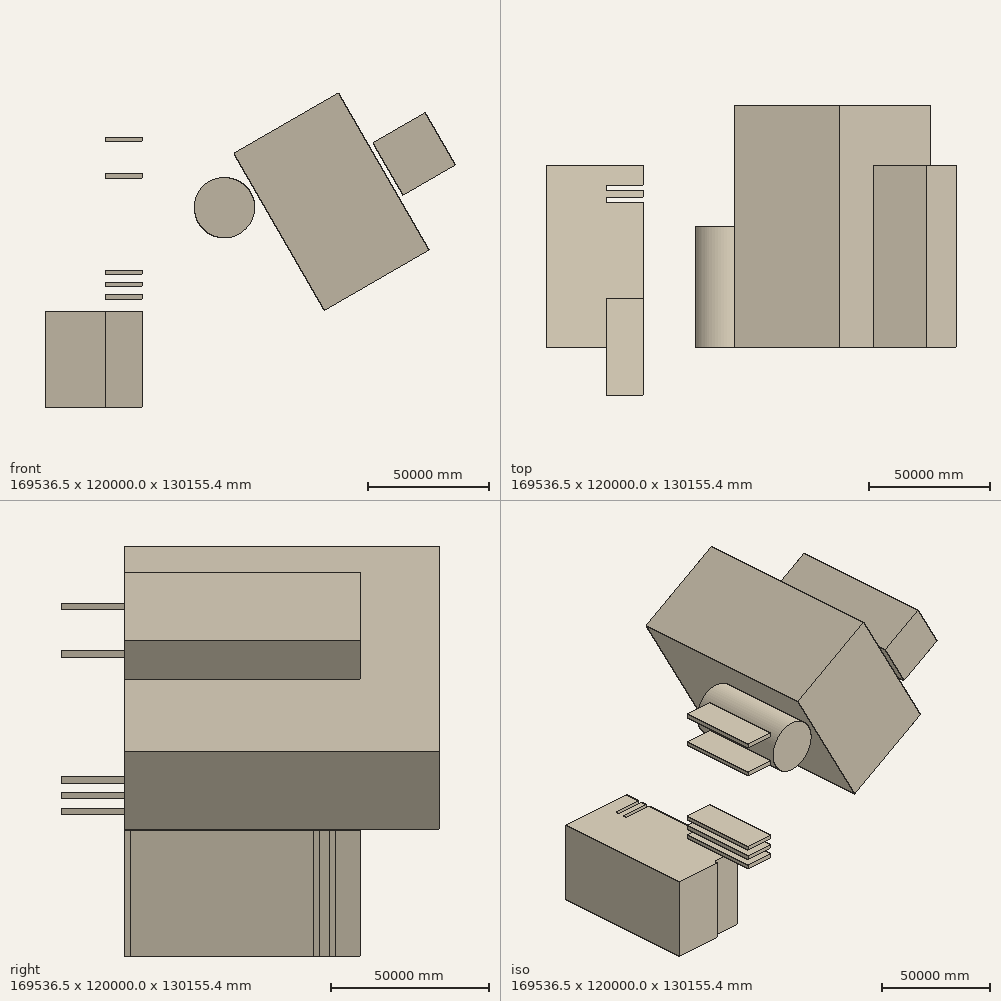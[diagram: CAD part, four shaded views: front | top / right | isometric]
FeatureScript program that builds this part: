
annotation { "Feature Type Name" : "Feature", "Feature Type Description" : "" }
export const myFeature = defineFeature(function(context is Context, id is Id, definition is map)
    precondition{}
    {
        {
            var Q0;
            Q0=qCreatedBy(makeId("Top.planeOp"),FACE);
            var sketch = newSketch(context, id + "F0", { "sketchPlane" : qUnion([Q0])});
            skLineSegment(sketch, "E0.bottom", {"start": v(20000, -20000) * mm, "end": v(-20000, -20000) * mm});
            skLineSegment(sketch, "E0.top", {"start": v(20000, 20000) * mm, "end": v(-20000, 20000) * mm});
            skLineSegment(sketch, "E0.left", {"start": v(20000, -20000) * mm, "end": v(20000, 20000) * mm});
            skLineSegment(sketch, "E0.right", {"start": v(-20000, -20000) * mm, "end": v(-20000, 20000) * mm});
            skPoint(sketch, "E0.middle", {"position": v(0, 0) * mm});
            skSolve(sketch);
        }
        {
            var Q0;
            Q0=makeQuery(id+"F0.imprint","IMPRINT",FACE,{"disambiguationData":[TD([[makeQuery(id+"F0.imprint","IMPRINT",EDGE,{"derivedFrom":sQuery(id+"F0.wireOp",EDGE,"E0.bottom")}),-1.0]])]});
            extrude(context, id + "F1", {"entities" : qUnion([Q0]), "depth" : 75000 * mm, "offsetDistance" : 25 * mm});
        }
        {
            var Q0;
            Q0=makeQuery(id+"F1.opExtrude","CAP_FACE",FACE,{"disambiguationData":[OSD([sQuery(id+"F0.wireOp",EDGE,"E0.bottom"),sQuery(id+"F0.wireOp",EDGE,"E0.top"),sQuery(id+"F0.wireOp",EDGE,"E0.left"),sQuery(id+"F0.wireOp",EDGE,"E0.right")])],"isStart":true});
            var sketch = newSketch(context, id + "F2", { "sketchPlane" : qUnion([Q0])});
            skLineSegment(sketch, "E1.bottom", {"start": v(20000, 20000) * mm, "end": v(5000, 20000) * mm});
            skLineSegment(sketch, "E1.top", {"start": v(20000, -20000) * mm, "end": v(5000, -20000) * mm});
            skLineSegment(sketch, "E1.left", {"start": v(20000, 20000) * mm, "end": v(20000, -20000) * mm});
            skLineSegment(sketch, "E1.right", {"start": v(5000, 20000) * mm, "end": v(5000, -20000) * mm});
            skSolve(sketch);
        }
        {
            var Q0;
            Q0=makeQuery(id+"F2.imprint","IMPRINT",FACE,{"disambiguationData":[TD([[makeQuery(id+"F2.imprint","IMPRINT",EDGE,{"derivedFrom":sQuery(id+"F2.wireOp",EDGE,"E1.bottom")}),1.0]])]});
            extrude(context, id + "F3", {"entities" : qUnion([Q0]), "oppositeDirection" : true, "depth" : 2000 * mm, "offsetDistance" : 25 * mm});
        }
        {
            var Q0;
            Q0=makeQuery(id+"F3.opExtrude","SWEPT_BODY",BODY,{"disambiguationData":[OSD([sQuery(id+"F2.wireOp",EDGE,"E1.bottom"),sQuery(id+"F2.wireOp",EDGE,"E1.top"),sQuery(id+"F2.wireOp",EDGE,"E1.left"),sQuery(id+"F2.wireOp",EDGE,"E1.right")])]});
            transform(context, id + "F4", {"entities" : qUnion([Q0]), "transformType" : TransformType.TRANSLATION_3D, "dx" : 0 * mm, "dy" : 0 * mm, "dz" : 5000 * mm, "makeCopy" : true});
        }
        {
            var Q0;
            Q0=makeQuery(id+"F4.opPattern","COPY",BODY,{"derivedFrom":makeQuery(id+"F3.opExtrude","SWEPT_BODY",BODY,{"disambiguationData":[OSD([sQuery(id+"F2.wireOp",EDGE,"E1.bottom"),sQuery(id+"F2.wireOp",EDGE,"E1.top"),sQuery(id+"F2.wireOp",EDGE,"E1.left"),sQuery(id+"F2.wireOp",EDGE,"E1.right")])]}),"instanceName":"1"});
            transform(context, id + "F5", {"entities" : qUnion([Q0]), "transformType" : TransformType.TRANSLATION_3D, "dx" : 0 * mm, "dy" : 0 * mm, "dz" : 5000 * mm, "makeCopy" : true});
        }
        {
            var Q0;
            Q0=makeQuery(id+"F5.opPattern","COPY",BODY,{"derivedFrom":makeQuery(id+"F4.opPattern","COPY",BODY,{"derivedFrom":makeQuery(id+"F3.opExtrude","SWEPT_BODY",BODY,{"disambiguationData":[OSD([sQuery(id+"F2.wireOp",EDGE,"E1.bottom"),sQuery(id+"F2.wireOp",EDGE,"E1.top"),sQuery(id+"F2.wireOp",EDGE,"E1.left"),sQuery(id+"F2.wireOp",EDGE,"E1.right")])]}),"instanceName":"1"}),"instanceName":"1"});
            transform(context, id + "F6", {"entities" : qUnion([Q0]), "transformType" : TransformType.TRANSLATION_3D, "dx" : 0 * mm, "dy" : 0 * mm, "dz" : 5000 * mm, "makeCopy" : true});
        }
        {
            var Q0;
            Q0=makeQuery(id+"F3.opExtrude","SWEPT_BODY",BODY,{"disambiguationData":[OSD([sQuery(id+"F2.wireOp",EDGE,"E1.bottom"),sQuery(id+"F2.wireOp",EDGE,"E1.top"),sQuery(id+"F2.wireOp",EDGE,"E1.left"),sQuery(id+"F2.wireOp",EDGE,"E1.right")])]});
            var Q1;
            Q1=makeQuery(id+"F4.opPattern","COPY",BODY,{"derivedFrom":makeQuery(id+"F3.opExtrude","SWEPT_BODY",BODY,{"disambiguationData":[OSD([sQuery(id+"F2.wireOp",EDGE,"E1.bottom"),sQuery(id+"F2.wireOp",EDGE,"E1.top"),sQuery(id+"F2.wireOp",EDGE,"E1.left"),sQuery(id+"F2.wireOp",EDGE,"E1.right")])]}),"instanceName":"1"});
            var Q2;
            Q2=makeQuery(id+"F5.opPattern","COPY",BODY,{"derivedFrom":makeQuery(id+"F4.opPattern","COPY",BODY,{"derivedFrom":makeQuery(id+"F3.opExtrude","SWEPT_BODY",BODY,{"disambiguationData":[OSD([sQuery(id+"F2.wireOp",EDGE,"E1.bottom"),sQuery(id+"F2.wireOp",EDGE,"E1.top"),sQuery(id+"F2.wireOp",EDGE,"E1.left"),sQuery(id+"F2.wireOp",EDGE,"E1.right")])]}),"instanceName":"1"}),"instanceName":"1"});
            var Q3;
            Q3=makeQuery(id+"F6.opPattern","COPY",BODY,{"derivedFrom":makeQuery(id+"F5.opPattern","COPY",BODY,{"derivedFrom":makeQuery(id+"F4.opPattern","COPY",BODY,{"derivedFrom":makeQuery(id+"F3.opExtrude","SWEPT_BODY",BODY,{"disambiguationData":[OSD([sQuery(id+"F2.wireOp",EDGE,"E1.bottom"),sQuery(id+"F2.wireOp",EDGE,"E1.top"),sQuery(id+"F2.wireOp",EDGE,"E1.left"),sQuery(id+"F2.wireOp",EDGE,"E1.right")])]}),"instanceName":"1"}),"instanceName":"1"}),"instanceName":"1"});
            transform(context, id + "F7", {"entities" : qUnion([Q0, Q1, Q2, Q3]), "transformType" : TransformType.TRANSLATION_3D, "dx" : 0 * mm, "dy" : 0 * mm, "dz" : 55000 * mm, "makeCopy" : true});
        }
        {
            var Q0;
            Q0=makeQuery(id+"F3.opExtrude","SWEPT_BODY",BODY,{"disambiguationData":[OSD([sQuery(id+"F2.wireOp",EDGE,"E1.bottom"),sQuery(id+"F2.wireOp",EDGE,"E1.top"),sQuery(id+"F2.wireOp",EDGE,"E1.left"),sQuery(id+"F2.wireOp",EDGE,"E1.right")])]});
            var Q1;
            Q1=makeQuery(id+"F7.opPattern","COPY",BODY,{"derivedFrom":makeQuery(id+"F5.opPattern","COPY",BODY,{"derivedFrom":makeQuery(id+"F4.opPattern","COPY",BODY,{"derivedFrom":makeQuery(id+"F3.opExtrude","SWEPT_BODY",BODY,{"disambiguationData":[OSD([sQuery(id+"F2.wireOp",EDGE,"E1.bottom"),sQuery(id+"F2.wireOp",EDGE,"E1.top"),sQuery(id+"F2.wireOp",EDGE,"E1.left"),sQuery(id+"F2.wireOp",EDGE,"E1.right")])]}),"instanceName":"1"}),"instanceName":"1"}),"instanceName":"1"});
            var Q2;
            Q2=makeQuery(id+"F7.opPattern","COPY",BODY,{"derivedFrom":makeQuery(id+"F4.opPattern","COPY",BODY,{"derivedFrom":makeQuery(id+"F3.opExtrude","SWEPT_BODY",BODY,{"disambiguationData":[OSD([sQuery(id+"F2.wireOp",EDGE,"E1.bottom"),sQuery(id+"F2.wireOp",EDGE,"E1.top"),sQuery(id+"F2.wireOp",EDGE,"E1.left"),sQuery(id+"F2.wireOp",EDGE,"E1.right")])]}),"instanceName":"1"}),"instanceName":"1"});
            var Q3;
            Q3=makeQuery(id+"F1.opExtrude","SWEPT_BODY",BODY,{"disambiguationData":[OSD([sQuery(id+"F0.wireOp",EDGE,"E0.bottom"),sQuery(id+"F0.wireOp",EDGE,"E0.top"),sQuery(id+"F0.wireOp",EDGE,"E0.left"),sQuery(id+"F0.wireOp",EDGE,"E0.right")])]});
            booleanBodies(context, id + "F8", {"operationType" : BooleanOperationType.SUBTRACTION, "tools" : qUnion([Q0, Q1, Q2]), "targets" : qUnion([Q3])});
        }
        {
            var Q0;
            Q0=qCreatedBy(makeId("Top.planeOp"),FACE);
            var sketch = newSketch(context, id + "F9", { "sketchPlane" : qUnion([Q0])});
            skLineSegment(sketch, "E2.bottom", {"start": v(130000, -37500) * mm, "end": v(80000, -37500) * mm});
            skLineSegment(sketch, "E2.top", {"start": v(130000, 37500) * mm, "end": v(80000, 37500) * mm});
            skLineSegment(sketch, "E2.left", {"start": v(130000, -37500) * mm, "end": v(130000, 37500) * mm});
            skLineSegment(sketch, "E2.right", {"start": v(80000, -37500) * mm, "end": v(80000, 37500) * mm});
            skPoint(sketch, "E2.middle", {"position": v(105000, 0) * mm});
            skLineSegment(sketch, "E3.bottom", {"start": v(157000, 12500) * mm, "end": v(132000, 12500) * mm});
            skLineSegment(sketch, "E3.top", {"start": v(157000, -12500) * mm, "end": v(132000, -12500) * mm});
            skLineSegment(sketch, "E3.left", {"start": v(157000, 12500) * mm, "end": v(157000, -12500) * mm});
            skLineSegment(sketch, "E3.right", {"start": v(132000, 12500) * mm, "end": v(132000, -12500) * mm});
            skPoint(sketch, "E3.middle", {"position": v(144500, 0) * mm});
            skCircle(sketch, "E4", {"center": v(65500, -20000) * mm, "radius": 12500 * mm});
            skSolve(sketch);
        }
        {
            var Q0;
            Q0=makeQuery(id+"F9.imprint","IMPRINT",FACE,{"disambiguationData":[TD([[makeQuery(id+"F9.imprint","IMPRINT",EDGE,{"derivedFrom":sQuery(id+"F9.wireOp",EDGE,"E4")}),1.0]])]});
            extrude(context, id + "F10", {"entities" : qUnion([Q0]), "depth" : 50000 * mm, "offsetDistance" : 25 * mm});
        }
        {
            var Q0;
            Q0=makeQuery(id+"F9.imprint","IMPRINT",FACE,{"disambiguationData":[TD([[makeQuery(id+"F9.imprint","IMPRINT",EDGE,{"derivedFrom":sQuery(id+"F9.wireOp",EDGE,"E2.bottom")}),-1.0]])]});
            extrude(context, id + "F11", {"entities" : qUnion([Q0]), "depth" : 100000 * mm, "offsetDistance" : 25 * mm});
        }
        {
            var Q0;
            Q0=makeQuery(id+"F9.imprint","IMPRINT",FACE,{"disambiguationData":[TD([[makeQuery(id+"F9.imprint","IMPRINT",EDGE,{"derivedFrom":sQuery(id+"F9.wireOp",EDGE,"E3.bottom")}),1.0]])]});
            extrude(context, id + "F12", {"entities" : qUnion([Q0]), "depth" : 75000 * mm, "offsetDistance" : 25 * mm});
        }
        {
            var Q0;
            Q0=makeQuery(id+"F1.opExtrude","SWEPT_BODY",BODY,{"disambiguationData":[OSD([sQuery(id+"F0.wireOp",EDGE,"E0.bottom"),sQuery(id+"F0.wireOp",EDGE,"E0.top"),sQuery(id+"F0.wireOp",EDGE,"E0.left"),sQuery(id+"F0.wireOp",EDGE,"E0.right")])]});
            var Q1;
            Q1=makeQuery(id+"F10.opExtrude","SWEPT_BODY",BODY,{"disambiguationData":[OSD([sQuery(id+"F9.wireOp",EDGE,"E4")])]});
            var Q2;
            Q2=makeQuery(id+"F11.opExtrude","SWEPT_BODY",BODY,{"disambiguationData":[OSD([sQuery(id+"F9.wireOp",EDGE,"E2.bottom"),sQuery(id+"F9.wireOp",EDGE,"E2.top"),sQuery(id+"F9.wireOp",EDGE,"E2.left"),sQuery(id+"F9.wireOp",EDGE,"E2.right")])]});
            var Q3;
            Q3=makeQuery(id+"F12.opExtrude","SWEPT_BODY",BODY,{"disambiguationData":[OSD([sQuery(id+"F9.wireOp",EDGE,"E3.bottom"),sQuery(id+"F9.wireOp",EDGE,"E3.top"),sQuery(id+"F9.wireOp",EDGE,"E3.left"),sQuery(id+"F9.wireOp",EDGE,"E3.right")])]});
            var Q4;
            Q4=sQuery(id+"F0.wireOp",EDGE,"E0.bottom");
            transform(context, id + "F13", {"entities" : qUnion([Q0, Q1, Q2, Q3]), "transformType" : TransformType.ROTATION, "transformAxis" : qUnion([Q4]), "angle" : 90 * degree, "makeCopy" : false});
        }
        {
            var Q0;
            Q0=makeQuery(id+"F11.opExtrude","SWEPT_BODY",BODY,{"disambiguationData":[OSD([sQuery(id+"F9.wireOp",EDGE,"E2.bottom"),sQuery(id+"F9.wireOp",EDGE,"E2.top"),sQuery(id+"F9.wireOp",EDGE,"E2.left"),sQuery(id+"F9.wireOp",EDGE,"E2.right")])]});
            var Q1;
            Q1=makeQuery(id+"F10.opExtrude","SWEPT_BODY",BODY,{"disambiguationData":[OSD([sQuery(id+"F9.wireOp",EDGE,"E4")])]});
            var Q2;
            Q2=makeQuery(id+"F12.opExtrude","SWEPT_BODY",BODY,{"disambiguationData":[OSD([sQuery(id+"F9.wireOp",EDGE,"E3.bottom"),sQuery(id+"F9.wireOp",EDGE,"E3.top"),sQuery(id+"F9.wireOp",EDGE,"E3.left"),sQuery(id+"F9.wireOp",EDGE,"E3.right")])]});
            var Q3;
            Q3=makeQuery(id+"F1.opExtrude","SWEPT_EDGE",EDGE,{"disambiguationData":[OSD([sQuery(id+"F0.wireOp",EDGE,"E0.bottom"),sQuery(id+"F0.wireOp",EDGE,"E0.right")])]});
            transform(context, id + "F14", {"entities" : qUnion([Q0, Q1, Q2]), "transformType" : TransformType.ROTATION, "transformAxis" : qUnion([Q3]), "angle" : 30 * degree, "makeCopy" : false});
        }
        {
            var Q0;
            Q0=makeQuery(id+"F1.opExtrude","SWEPT_BODY",BODY,{"disambiguationData":[OSD([sQuery(id+"F0.wireOp",EDGE,"E0.bottom"),sQuery(id+"F0.wireOp",EDGE,"E0.top"),sQuery(id+"F0.wireOp",EDGE,"E0.left"),sQuery(id+"F0.wireOp",EDGE,"E0.right")])]});
            var Q1;
            Q1=makeQuery(id+"F11.opExtrude","SWEPT_BODY",BODY,{"disambiguationData":[OSD([sQuery(id+"F9.wireOp",EDGE,"E2.bottom"),sQuery(id+"F9.wireOp",EDGE,"E2.top"),sQuery(id+"F9.wireOp",EDGE,"E2.left"),sQuery(id+"F9.wireOp",EDGE,"E2.right")])]});
            var Q2;
            Q2=makeQuery(id+"F10.opExtrude","SWEPT_BODY",BODY,{"disambiguationData":[OSD([sQuery(id+"F9.wireOp",EDGE,"E4")])]});
            var Q3;
            Q3=makeQuery(id+"F12.opExtrude","SWEPT_BODY",BODY,{"disambiguationData":[OSD([sQuery(id+"F9.wireOp",EDGE,"E3.bottom"),sQuery(id+"F9.wireOp",EDGE,"E3.top"),sQuery(id+"F9.wireOp",EDGE,"E3.left"),sQuery(id+"F9.wireOp",EDGE,"E3.right")])]});
            transform(context, id + "F15", {"entities" : qUnion([Q0, Q1, Q2, Q3]), "transformType" : TransformType.TRANSLATION_3D, "dx" : 0 * mm, "dy" : 20000 * mm, "dz" : 0 * mm, "makeCopy" : false});
        }
    });
